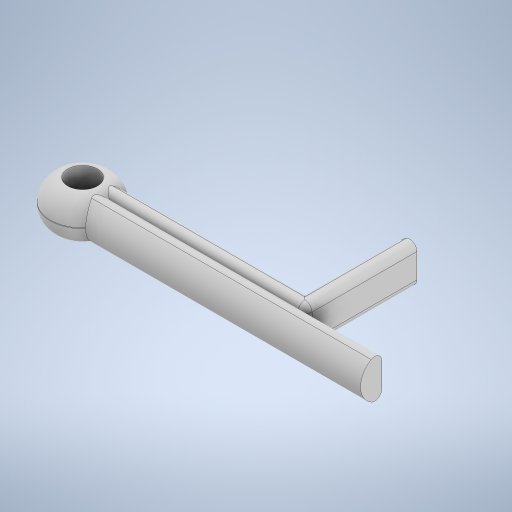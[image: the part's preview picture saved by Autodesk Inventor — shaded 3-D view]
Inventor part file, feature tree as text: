
AUTODESK INVENTOR PART (.ipt)
format: ipt  version: 2023 (Build 270158000, 158)  size: 333,312 bytes
history: native  units: in
note: dims shown in document units (in); Inventor stores cm internally (conversion verified against a paired STEP export)
features: fillet x5, extrude x2, sketch x1
ambient origin geometry x8: Origin, YZ Plane, XZ Plane, XY Plane, X Axis, Y Axis, Z Axis, Center Point
bodies: Solid1 (feature_tree)
feature tree (8):
  sketch  "Sketch5"  dims[d5=0.03in d6=0.06in d7=0.0in d10=0.03in d11=0.01in d16=0.01in d17=0.06in d18=0.0in d19=0.03in d20=0.01in d12=0.0in d13=0.0in d14=0.0in]
  extrude  "Extrusion1"  Depth=0.01in TaperAngle=0.0deg
  fillet  "Fillet1"  Radius=0.03in
  fillet  "Fillet2"  Radius=0.01in
  fillet  "Fillet5"  Radius=0.01in
  extrude  "Extrusion4"  Depth=0.01in TaperAngle=0.0deg
  fillet  "Fillet6"  Radius=0.03in
  fillet  "Fillet7"  Radius=0.01in
